# Revit family: METALFIRE_ULTIMATE_D_MF_WHE_3S
name_source: partatom
category: Mechanical Equipment
revit_build: Autodesk Revit 2017 (Build: 20160225_1515(x64)
units: mm (PartAtom-declared; Revit-internal decimal feet)

## family parameters
Always vertical = Yes
Cut with Voids When Loaded = No
Host = Wall
OmniClass Number = 23.75.00.00
OmniClass Title = Climate Control (HVAC)
Part Type = Normal
Room Calculation Point = Yes
Round Connector Dimension = Use Diameter
Shared = No

## types (2) — shared parameters
BIM BADGE = https://bim.archiproducts.com
CO EMISSION = 0.09%
DEPTH = 461 mm
Description = This generation of room air independent wood fireplaces with liftable door is equipped with a dynamic combustion technique that ensures optimal combustion and high efficiency.
EFFICIENCY = 82.00%
ENERGY EFFICIENCY CLASS = A+
FINISHING MATERIAL = Black painted vermiculite plates - Metalfire
FRAME MATERIAL = Iron - Metalfire
HEIGHT = 504 mm
MATERIAL DESCRIPTION = Iron, galvanized steel and vermiculite plates
Manufacturer = Metalfire
Model = Ultime D
OVERALL DEPTH = 608 mm
OVERALL HEIGHT = 1443 mm
PRODUCT SHEET = https://www.archiproducts.com
SMOKE EXHAUST = Ø250 mm
TECHNICAL SHEET = https://www.metalfire.eu
URL = https://www.metalfire.eu
WEIGHT = 320.00 kg

## per-type parameters (varying)
| type | FINE DUST EMISSION | OUTPUT | OVERALL WIDTH | PRODUCT CODE | WIDTH |
| 800 x 500 mm | 10 mg/Nm3 | 16.0 kW | 868 mm | MF 800-50 WHE 3S | 868 mm |
| 1050 x 500 mm | 27 mg/Nm3 | 17.0 kW | 1118 mm | MF 1050-50 WHE 3S | 1118 mm |

## geometry (parser evidence)
native form markers: Sweep x5
no freeform markers — native parametric forms only
